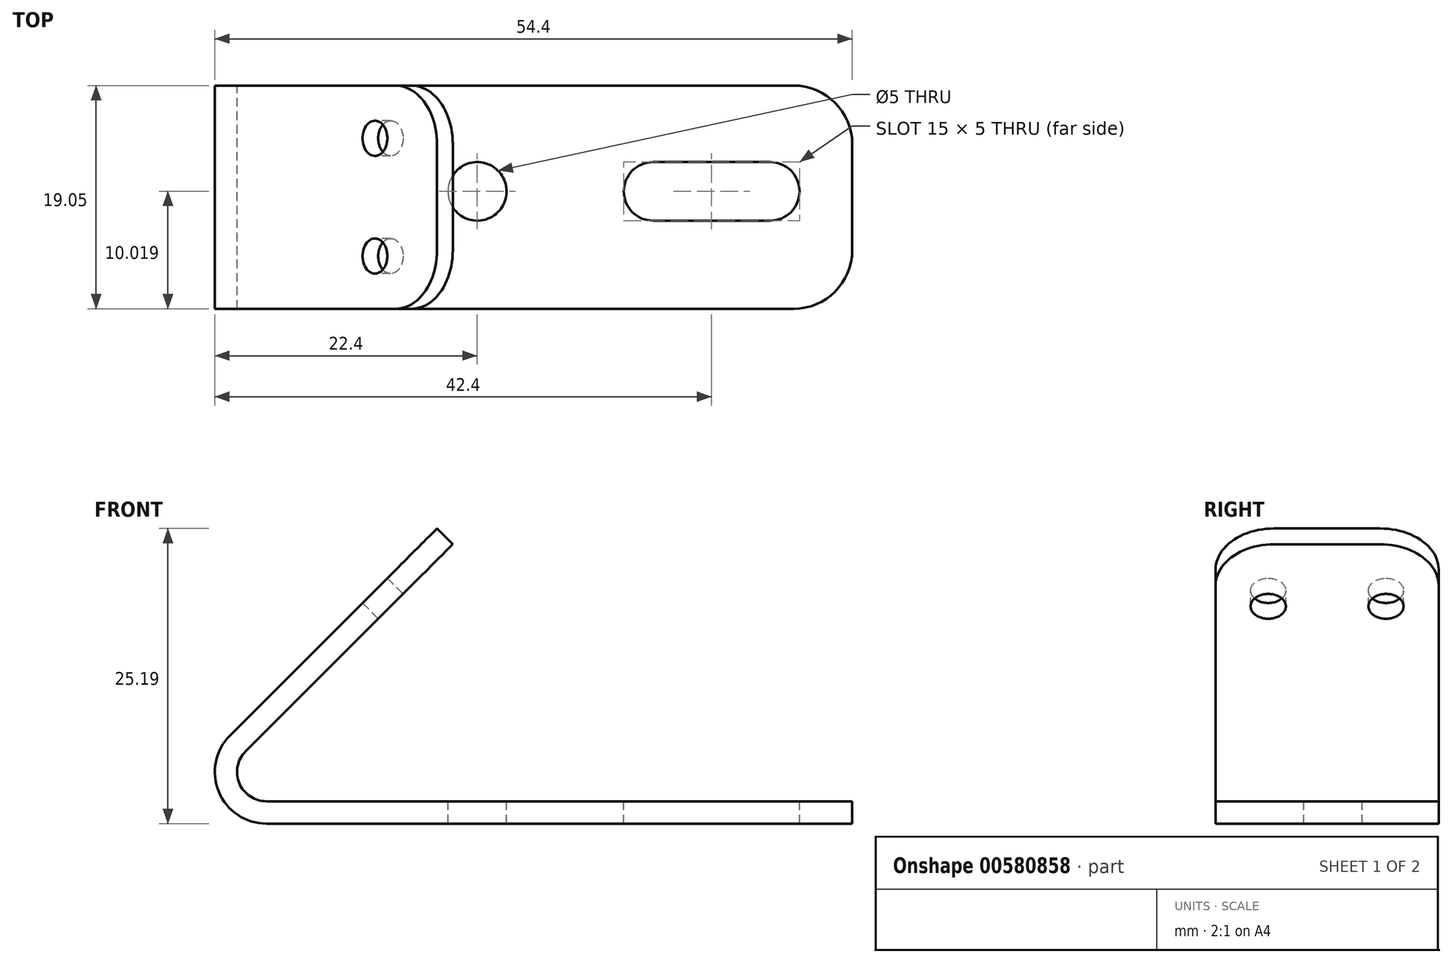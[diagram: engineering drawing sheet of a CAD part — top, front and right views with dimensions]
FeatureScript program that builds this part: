
annotation { "Feature Type Name" : "Feature", "Feature Type Description" : "" }
export const myFeature = defineFeature(function(context is Context, id is Id, definition is map)
    precondition{}
    {
        {
            var Q0;
            Q0=qCreatedBy(makeId("Front.planeOp"),FACE);
            var sketch = newSketch(context, id + "F0", { "sketchPlane" : qUnion([Q0])});
            skArc(sketch, "E0", {"start": v(-3.11, 3.11) * mm, "mid": v(-4.07, -1.68) * mm, "end": v(0, -4.4) * mm});
            skLineSegment(sketch, "E1", {"start": v(14.57, 20.79) * mm, "end": v(-3.11, 3.11) * mm});
            skLineSegment(sketch, "E2", {"start": v(0, -4.4) * mm, "end": v(50, -4.4) * mm});
            skLineSegment(sketch, "E3.0", {"start": v(0, -2.5) * mm, "end": v(50, -2.5) * mm});
            skArc(sketch, "E3.1", {"start": v(-1.77, 1.77) * mm, "mid": v(-2.3, -0.96) * mm, "end": v(0, -2.5) * mm});
            skLineSegment(sketch, "E3.2", {"start": v(15.9, 19.45) * mm, "end": v(-1.77, 1.77) * mm});
            skLineSegment(sketch, "E4", {"start": v(14.57, 20.79) * mm, "end": v(15.9, 19.45) * mm});
            skLineSegment(sketch, "E5", {"start": v(50, -2.5) * mm, "end": v(50, -4.4) * mm});
            skSolve(sketch);
        }
        {
            var Q0;
            Q0=qSketchRegion(id+"F0",true);
            extrude(context, id + "F1", {"entities" : qUnion([Q0]), "depth" : 19.05 * mm, "offsetDistance" : 25 * mm});
        }
        {
            var Q0;
            Q0=makeQuery(id+"F1.opExtrude","SWEPT_FACE",FACE,{"disambiguationData":[OSD([sQuery(id+"F0.wireOp",EDGE,"E3.0")])]});
            var sketch = newSketch(context, id + "F2", { "sketchPlane" : qUnion([Q0])});
            skCircle(sketch, "E6", {"center": v(18, -9.03) * mm, "radius": 2.5 * mm});
            skLineSegment(sketch, "E7.bottom", {"start": v(43, -11.53) * mm, "end": v(33, -11.53) * mm});
            skLineSegment(sketch, "E7.top", {"start": v(43, -6.53) * mm, "end": v(33, -6.53) * mm});
            skPoint(sketch, "E7.middle", {"position": v(38, -9.03) * mm});
            skArc(sketch, "E8", {"start": v(33, -6.53) * mm, "mid": v(30.5, -9.03) * mm, "end": v(33, -11.53) * mm});
            skArc(sketch, "E9", {"start": v(43, -11.53) * mm, "mid": v(45.5, -9.03) * mm, "end": v(43, -6.53) * mm});
            skSolve(sketch);
        }
        {
            var Q0;
            Q0=qSketchRegion(id+"F2",true);
            extrude(context, id + "F3", {"entities" : qUnion([Q0]), "operationType" : NewBodyOperationType.REMOVE, "endBound" : BoundingType.THROUGH_ALL, "oppositeDirection" : true, "depth" : 25 * mm, "offsetDistance" : 25 * mm});
        }
        {
            var Q0;
            Q0=makeQuery(id+"F1.opExtrude","CAP_EDGE",EDGE,{"disambiguationData":[OSD([sQuery(id+"F0.wireOp",EDGE,"E5")])],"isStart":false});
            var Q1;
            Q1=makeQuery(id+"F1.opExtrude","CAP_EDGE",EDGE,{"disambiguationData":[OSD([sQuery(id+"F0.wireOp",EDGE,"E5")])],"isStart":true});
            fillet(context, id + "F4", {"entities" : qUnion([Q0, Q1]), "radius" : 5 * mm, "tangentPropagation" : true, "allowEdgeOverflow" : false});
        }
        {
            var Q0;
            Q0=makeQuery(id+"F1.opExtrude","CAP_EDGE",EDGE,{"disambiguationData":[OSD([sQuery(id+"F0.wireOp",EDGE,"E4")])],"isStart":false});
            var Q1;
            Q1=makeQuery(id+"F1.opExtrude","CAP_EDGE",EDGE,{"disambiguationData":[OSD([sQuery(id+"F0.wireOp",EDGE,"E4")])],"isStart":true});
            fillet(context, id + "F5", {"entities" : qUnion([Q0, Q1]), "radius" : 5 * mm, "tangentPropagation" : true, "allowEdgeOverflow" : false});
        }
        {
            var Q0;
            Q0=makeQuery(id+"F1.opExtrude","SWEPT_FACE",FACE,{"disambiguationData":[OSD([sQuery(id+"F0.wireOp",EDGE,"E1")])]});
            var sketch = newSketch(context, id + "F6", { "sketchPlane" : qUnion([Q0])});
            skCircle(sketch, "E10", {"center": v(4.5, 17.5) * mm, "radius": 1.5 * mm});
            skCircle(sketch, "E11", {"center": v(14.55, 17.5) * mm, "radius": 1.5 * mm});
            skSolve(sketch);
        }
        {
            var Q0;
            Q0=qSketchRegion(id+"F6",true);
            var Q1;
            Q1=makeQuery(id+"F1.opExtrude","SWEPT_FACE",FACE,{"disambiguationData":[OSD([sQuery(id+"F0.wireOp",EDGE,"E3.2")])]});
            extrude(context, id + "F7", {"entities" : qUnion([Q0]), "operationType" : NewBodyOperationType.REMOVE, "endBound" : BoundingType.UP_TO_SURFACE, "oppositeDirection" : true, "depth" : 25 * mm, "endBoundEntityFace" : qUnion([Q1]), "offsetDistance" : 25 * mm});
        }
    });
